FCSTD DOCUMENT  (FreeCAD 0.19R0.19.2)
Label: v0_01
License: All rights reserved
LicenseURL: http://en.wikipedia.org/wiki/All_rights_reserved
objects: Sketcher::SketchObject×1
note: 1 computed .brp shape members not serialized (recipe doc carries the construction recipe); baked Part::Feature solids carry a one-line shape summary decoded from their .brp

FEATURE [Sketcher::SketchObject] Sketch
  FullyConstrained = true
  sketch-geometry (11):
    g0: LineSegment StartX=0 StartY=0 StartZ=0 EndX=111.35 EndY=0 EndZ=0
    g1: Circle CenterX=111.35 CenterY=-15.15 CenterZ=0 NormalX=0 NormalY=0 NormalZ=1 AngleXU=0 Radius=3.25
    g2: LineSegment StartX=111.35 StartY=0 StartZ=0 EndX=144.4 EndY=0 EndZ=0
    g3: LineSegment StartX=144.4 StartY=0 StartZ=0 EndX=144.4 EndY=-7 EndZ=0
    g4: LineSegment StartX=144.9 StartY=-7.5 StartZ=0 EndX=151.9 EndY=-7.5 EndZ=0
    g5: ArcOfCircle CenterX=144.9 CenterY=-7 CenterZ=0 NormalX=0 NormalY=0 NormalZ=1 AngleXU=0 Radius=0.5 StartAngle=3.1416 EndAngle=4.71239
    g6: LineSegment StartX=111.35 StartY=0 StartZ=0 EndX=98.1 EndY=0 EndZ=0
    g7: LineSegment StartX=98.1 StartY=0 StartZ=0 EndX=98.1 EndY=-4.9 EndZ=0
    g8: Circle CenterX=98.1 CenterY=-6.2 CenterZ=0 NormalX=0 NormalY=0 NormalZ=1 AngleXU=0 Radius=1.3
    g9: LineSegment StartX=99.4 StartY=-6.2 StartZ=0 EndX=98.1 EndY=-6.2 EndZ=0
    g10: LineSegment StartX=81.9 StartY=-6.2 StartZ=0 EndX=99.4 EndY=-6.2 EndZ=0
  constraints (30):
    c: Coincident(g0,g-1)
    c: PointOnObject(g0,g-1)
    c: Distance(g0) = 111.35
    c: Radius(g1) = 3.25
    c: Block(g1)
    c: Horizontal(g2)
    c: Distance(g2) = 33.05
    c: Coincident(g2,g0)
    c: Vertical(g3)
    c: Distance(g3) = 7
    c: Coincident(g3,g2)
    c: Horizontal(g4)
    c: Distance(g4) = 7
    c: Coincident(g5,g3)
    c: Coincident(g5,g4)
    c: Block(g5)
    c: Horizontal(g6)
    c: Distance(g6) = 13.25
    c: Coincident(g6,g0)
    c: Vertical(g7)
    c: Distance(g7) = 4.9
    c: Coincident(g7,g6)
    c: PointOnObject(g7,g8)
    c: Block(g8)
    c: Horizontal(g9)
    c: Distance(g9) = 1.3
    c: Coincident(g9,g8)
    c: Horizontal(g10)
    c: Distance(g10) = 17.5
    c: Coincident(g10,g9)
